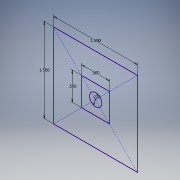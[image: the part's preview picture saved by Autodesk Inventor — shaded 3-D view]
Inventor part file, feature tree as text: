
AUTODESK INVENTOR PART (.ipt)
format: ipt  version: 2016 (Build 200138000, 138)  size: 88,064 bytes
history: native  units: in
note: dims shown in document units (in); Inventor stores cm internally (conversion verified against a paired STEP export)
features: sketch x1
ambient origin geometry x8: Origin, YZ Plane, XZ Plane, XY Plane, X Axis, Y Axis, Z Axis, Center Point
feature tree (1):
  sketch  "Sketch1"  dims[d0=0.22in d1=1.5in d2=1.5in d3=0.5in d4=0.5in]
